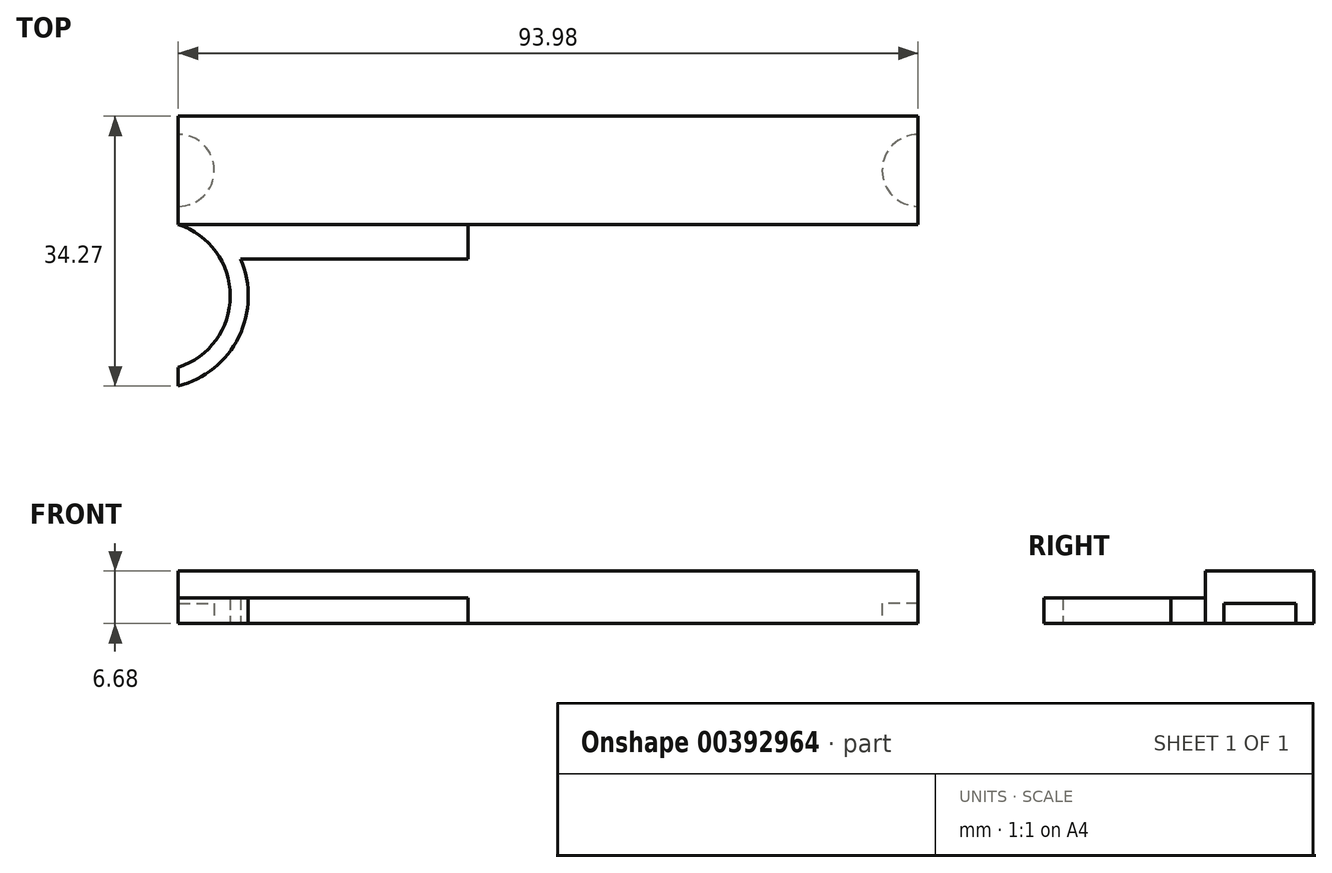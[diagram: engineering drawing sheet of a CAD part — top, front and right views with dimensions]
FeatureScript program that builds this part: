
annotation { "Feature Type Name" : "Feature", "Feature Type Description" : "" }
export const myFeature = defineFeature(function(context is Context, id is Id, definition is map)
    precondition{}
    {
        {
            var Q0;
            Q0=qCreatedBy(makeId("Top.planeOp"),FACE);
            var sketch = newSketch(context, id + "F0", { "sketchPlane" : qUnion([Q0])});
            skLineSegment(sketch, "E0.bottom", {"start": v(-47, 18.16) * mm, "end": v(47, 18.16) * mm});
            skLineSegment(sketch, "E0.top", {"start": v(-39.06, 0) * mm, "end": v(-10.16, 0) * mm});
            skLineSegment(sketch, "E0.left", {"start": v(-47, 18.16) * mm, "end": v(-47, 4.4) * mm});
            skLineSegment(sketch, "E0.right", {"start": v(47, 18.16) * mm, "end": v(47, 4.4) * mm});
            skArc(sketch, "E1", {"start": v(-47, -13.73) * mm, "mid": v(-40.39, -4.66) * mm, "end": v(-47, 4.4) * mm});
            skArc(sketch, "E2", {"start": v(-47, -16.1) * mm, "mid": v(-39.31, -9.88) * mm, "end": v(-39.06, 0) * mm});
            skArc(sketch, "E3.MirrorCS", {"start": v(47, -16.1) * mm, "mid": v(39.31, -9.88) * mm, "end": v(39.06, 0) * mm});
            skArc(sketch, "E4.MirrorCS", {"start": v(47, -13.73) * mm, "mid": v(40.39, -4.66) * mm, "end": v(47, 4.4) * mm});
            skPoint(sketch, "E5.orphan", {"position": v(47, 0) * mm});
            skLineSegment(sketch, "E6.bottom", {"start": v(10.16, 4.4) * mm, "end": v(-10.16, 4.4) * mm});
            skLineSegment(sketch, "E6.left", {"start": v(10.16, 4.4) * mm, "end": v(10.16, 0) * mm});
            skLineSegment(sketch, "E6.right", {"start": v(-10.16, 4.4) * mm, "end": v(-10.16, 0) * mm});
            skPoint(sketch, "E6.middle", {"position": v(0, 0) * mm});
            skPoint(sketch, "E7.orphan", {"position": v(10.16, -4.4) * mm});
            skPoint(sketch, "E8.orphan", {"position": v(-10.16, -4.4) * mm});
            skLineSegment(sketch, "E9.trimOffspring", {"start": v(10.16, 0) * mm, "end": v(39.06, 0) * mm});
            skLineSegment(sketch, "E10.top", {"start": v(-47, 4.4) * mm, "end": v(47, 4.4) * mm});
            skLineSegment(sketch, "E11", {"start": v(-47, -13.73) * mm, "end": v(-47, -16.1) * mm});
            skLineSegment(sketch, "E12", {"start": v(47, 4.4) * mm, "end": v(47, 0) * mm});
            skLineSegment(sketch, "E13.trimOffspring", {"start": v(47, -13.73) * mm, "end": v(47, -16.1) * mm});
            skSolve(sketch);
        }
        {
            var Q0;
            Q0=makeQuery(id+"F0.imprint","IMPRINT",FACE,{"disambiguationData":[TD([[makeQuery(id+"F0.imprint","IMPRINT",EDGE,{"derivedFrom":sQuery(id+"F0.wireOp",EDGE,"E0.bottom")}),-1.0]])]});
            extrude(context, id + "F1", {"entities" : qUnion([Q0]), "depth" : 6.68 * mm, "offsetDistance" : 25.4 * mm});
        }
        {
            var Q0;
            Q0=makeQuery(id+"F0.imprint","IMPRINT",FACE,{"disambiguationData":[TD([[makeQuery(id+"F0.imprint","IMPRINT",EDGE,{"derivedFrom":sQuery(id+"F0.wireOp",EDGE,"E0.top")}),1.0]])]});
            var Q1;
            Q1=makeQuery(id+"F0.imprint","IMPRINT",FACE,{"disambiguationData":[TD([[makeQuery(id+"F0.imprint","IMPRINT",EDGE,{"derivedFrom":sQuery(id+"F0.wireOp",EDGE,"E3.MirrorCS")}),-1.0]])]});
            extrude(context, id + "F2", {"entities" : qUnion([Q0, Q1]), "operationType" : NewBodyOperationType.ADD, "depth" : 3.25 * mm, "offsetDistance" : 25.4 * mm});
        }
        {
            var Q0;
            Q0=makeQuery(id+"F0.imprint","IMPRINT",FACE,{"disambiguationData":[TD([[makeQuery(id+"F0.imprint","IMPRINT",EDGE,{"derivedFrom":sQuery(id+"F0.wireOp",EDGE,"E0.bottom")}),-1.0]])]});
            var sketch = newSketch(context, id + "F3", { "sketchPlane" : qUnion([Q0])});
            skArc(sketch, "E14", {"start": v(-47, 6.7) * mm, "mid": v(-42.42, 11.28) * mm, "end": v(-47, 15.85) * mm});
            skLineSegment(sketch, "E15", {"start": v(-47, 15.85) * mm, "end": v(-47, 6.7) * mm});
            skArc(sketch, "E16.MirrorCS", {"start": v(47, 6.7) * mm, "mid": v(42.42, 11.28) * mm, "end": v(47, 15.85) * mm});
            skLineSegment(sketch, "E17.MirrorCS", {"start": v(47, 15.85) * mm, "end": v(47, 6.7) * mm});
            skSolve(sketch);
        }
        {
            var Q0;
            Q0 = qSketchRegion(id + "F3", true);
            extrude(context, id + "F4", {"entities" : qUnion([Q0]), "operationType" : NewBodyOperationType.REMOVE, "depth" : 2.54 * mm, "offsetDistance" : 25.4 * mm});
        }
    });
